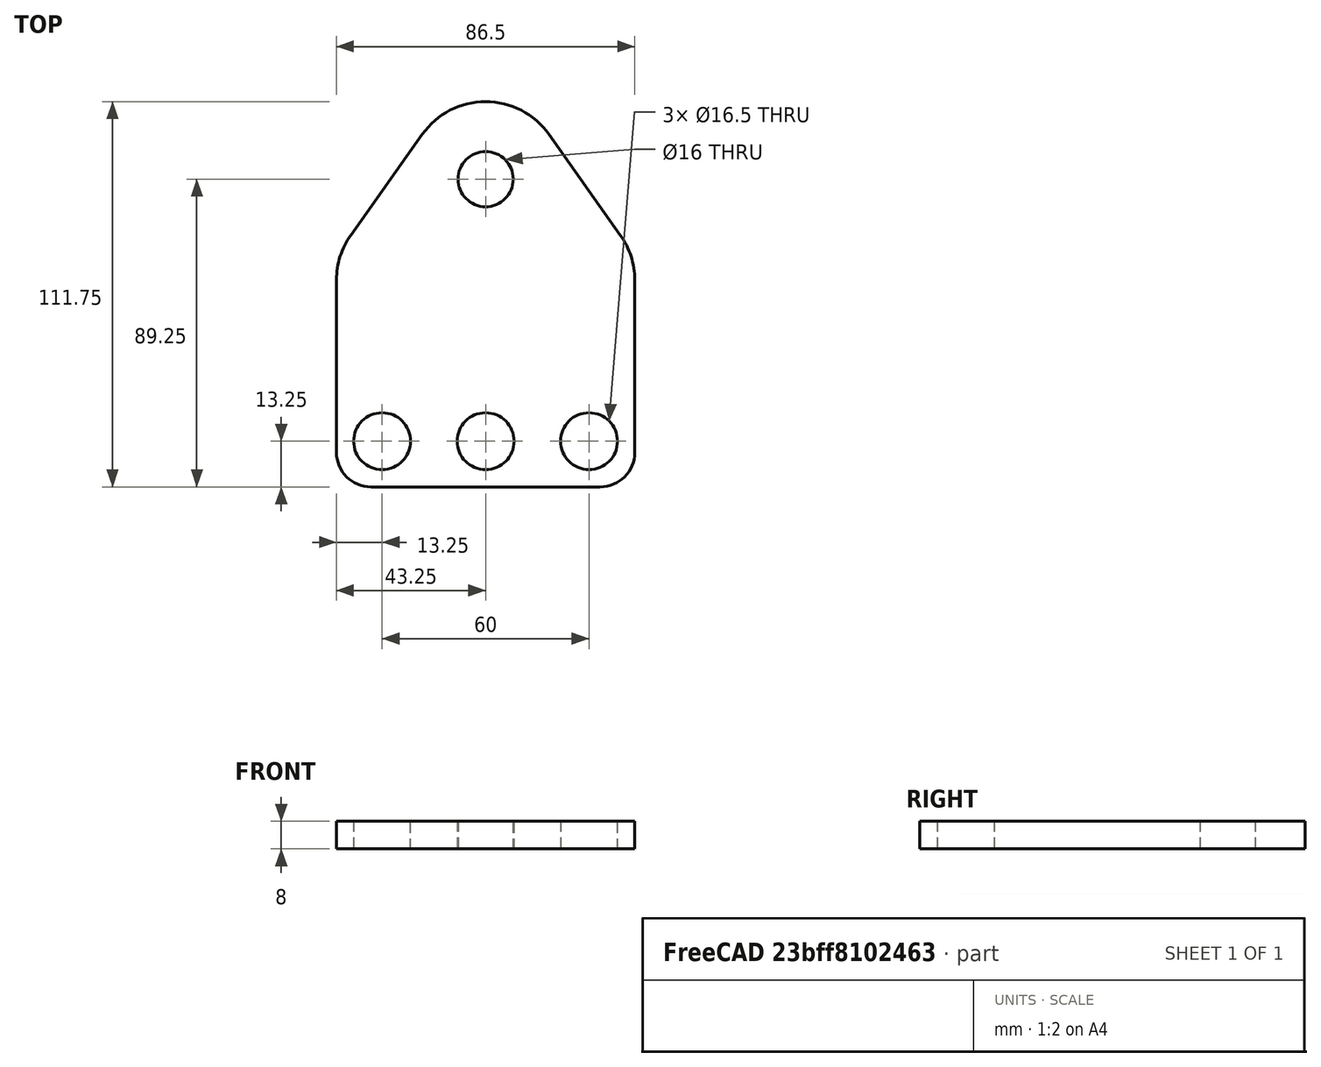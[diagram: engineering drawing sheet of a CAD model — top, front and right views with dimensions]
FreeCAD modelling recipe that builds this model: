
FCSTD DOCUMENT  (FreeCAD 0.19R24267 +99 (Git))
Label: V2 Allignment plate centre steady
License: All rights reserved
LicenseURL: http://en.wikipedia.org/wiki/All_rights_reserved
objects: Sketcher::SketchObject×1, PartDesign::Pad×1, PartDesign::Body×1
note: 4 computed .brp shape members not serialized (recipe doc carries the construction recipe); baked Part::Feature solids carry a one-line shape summary decoded from their .brp

FEATURE [Sketcher::SketchObject] Sketch
  FullyConstrained = true
  MapMode = 5
  Support = -> [XY_Plane]
  sketch-geometry (19):
    g0: Circle CenterX=0 CenterY=0 CenterZ=0 NormalX=0 NormalY=0 NormalZ=1 AngleXU=0 Radius=6
    g1: Circle CenterX=0 CenterY=0 CenterZ=0 NormalX=0 NormalY=0 NormalZ=1 AngleXU=0 Radius=8
    g2: Circle CenterX=0 CenterY=0 CenterZ=0 NormalX=0 NormalY=0 NormalZ=1 AngleXU=0 Radius=28
    g3: Circle CenterX=0 CenterY=-76 CenterZ=0 NormalX=0 NormalY=0 NormalZ=1 AngleXU=0 Radius=8.25
    g4: Circle CenterX=30 CenterY=-76 CenterZ=0 NormalX=0 NormalY=0 NormalZ=1 AngleXU=0 Radius=8.25
    g5: Circle CenterX=-30 CenterY=-76 CenterZ=0 NormalX=0 NormalY=0 NormalZ=1 AngleXU=0 Radius=8.25
    g6: LineSegment StartX=-30 StartY=-76 StartZ=0 EndX=30 EndY=-76 EndZ=0
    g7: LineSegment StartX=-43.25 StartY=-79.25 StartZ=0 EndX=-43.25 EndY=-29.25 EndZ=0
    g8: LineSegment StartX=-33.25 StartY=-89.25 StartZ=0 EndX=33.25 EndY=-89.25 EndZ=0
    g9: LineSegment StartX=43.25 StartY=-79.25 StartZ=0 EndX=43.25 EndY=-29.25 EndZ=0
    g10: ArcOfCircle CenterX=0 CenterY=0 CenterZ=0 NormalX=0 NormalY=0 NormalZ=1 AngleXU=0 Radius=22.5 StartAngle=0.617008 EndAngle=2.52458
    g11: LineSegment StartX=-39.1013 StartY=-16.2316 StartZ=0 EndX=-18.3513 EndY=13.0184 EndZ=0
    g12: LineSegment StartX=39.1013 StartY=-16.2316 StartZ=0 EndX=18.3513 EndY=13.0184 EndZ=0
    g13: ArcOfCircle CenterX=-33.25 CenterY=-79.25 CenterZ=0 NormalX=0 NormalY=0 NormalZ=1 AngleXU=0 Radius=10 StartAngle=3.14159 EndAngle=4.71239
    g14: ArcOfCircle CenterX=33.25 CenterY=-79.25 CenterZ=0 NormalX=0 NormalY=0 NormalZ=1 AngleXU=0 Radius=10 StartAngle=4.71239 EndAngle=6.28319
    g15: ArcOfCircle CenterX=20.75 CenterY=-29.25 CenterZ=0 NormalX=0 NormalY=0 NormalZ=1 AngleXU=0 Radius=22.5 StartAngle=0 EndAngle=0.617008
    g16: ArcOfCircle CenterX=-20.75 CenterY=-29.25 CenterZ=0 NormalX=0 NormalY=0 NormalZ=1 AngleXU=0 Radius=22.5 StartAngle=2.52458 EndAngle=3.14159
    g17: LineSegment StartX=30 StartY=-76 StartZ=0 EndX=43.25 EndY=-76 EndZ=0
    g18: LineSegment StartX=30 StartY=-76 StartZ=0 EndX=30 EndY=-89.25 EndZ=0
  constraints (45):
    c: Coincident(g0,g-1)
    c: Coincident(g1,g0)
    c: Diameter(g1) = 16
    c: Diameter(g0) = 12
    c: Coincident(g2,g0)
    c: Diameter(g2) = 56
    c: PointOnObject(g3,g-2)
    c: Coincident(g6,g5)
    c: Coincident(g6,g4)
    c: Horizontal(g6)
    c: Equal(g3,g5)
    c: Equal(g5,g4)
    c: Diameter(g5) = 16.5
    c: DistanceX(g6,g6) = 60
    c: Symmetric(g5,g4,g3)
    c: Vertical(g7)
    c: Vertical(g9)
    c: Coincident(g10,g0)
    c: Tangent(g10,g11) = 1.5708
    c: Tangent(g7,g13) = 1.5708
    c: Tangent(g8,g13) = -1.5708
    c: Tangent(g9,g14) = -1.5708
    c: Tangent(g8,g14) = -1.5708
    c: Tangent(g12,g15) = -1.5708
    c: Tangent(g9,g15) = -1.5708
    c: Tangent(g11,g16) = 1.5708
    c: Tangent(g7,g16) = 1.5708
    c: Equal(g13,g14)
    c: Symmetric(g8,g8,g-2)
    c: Radius(g13) = 10
    c: Coincident(g17,g4)
    c: PointOnObject(g17,g9)
    c: Horizontal(g17)
    c: Coincident(g18,g4)
    c: PointOnObject(g18,g8)
    c: Vertical(g18)
    c: Equal(g17,g18)
    c: DistanceX(g17,g17) = 13.25
    c: Equal(g16,g10)
    c: Equal(g10,g15)
    c: Diameter(g10) = 45
    c: Tangent(g10,g12) = -1.5708
    c: DistanceY(g3,g1) = 76
    c: Equal(g9,g7)
    c: DistanceY(g7,g7) = 50
FEATURE [PartDesign::Pad] Pad
  Direction = (1,1,1)
  Length = 8
  Length2 = 100
  Profile = -> Sketch
  Type = 0
FEATURE [PartDesign::Body] Body
  Group = -> [Sketch,Pad]
  Origin = -> Origin
  Tip = -> Pad
